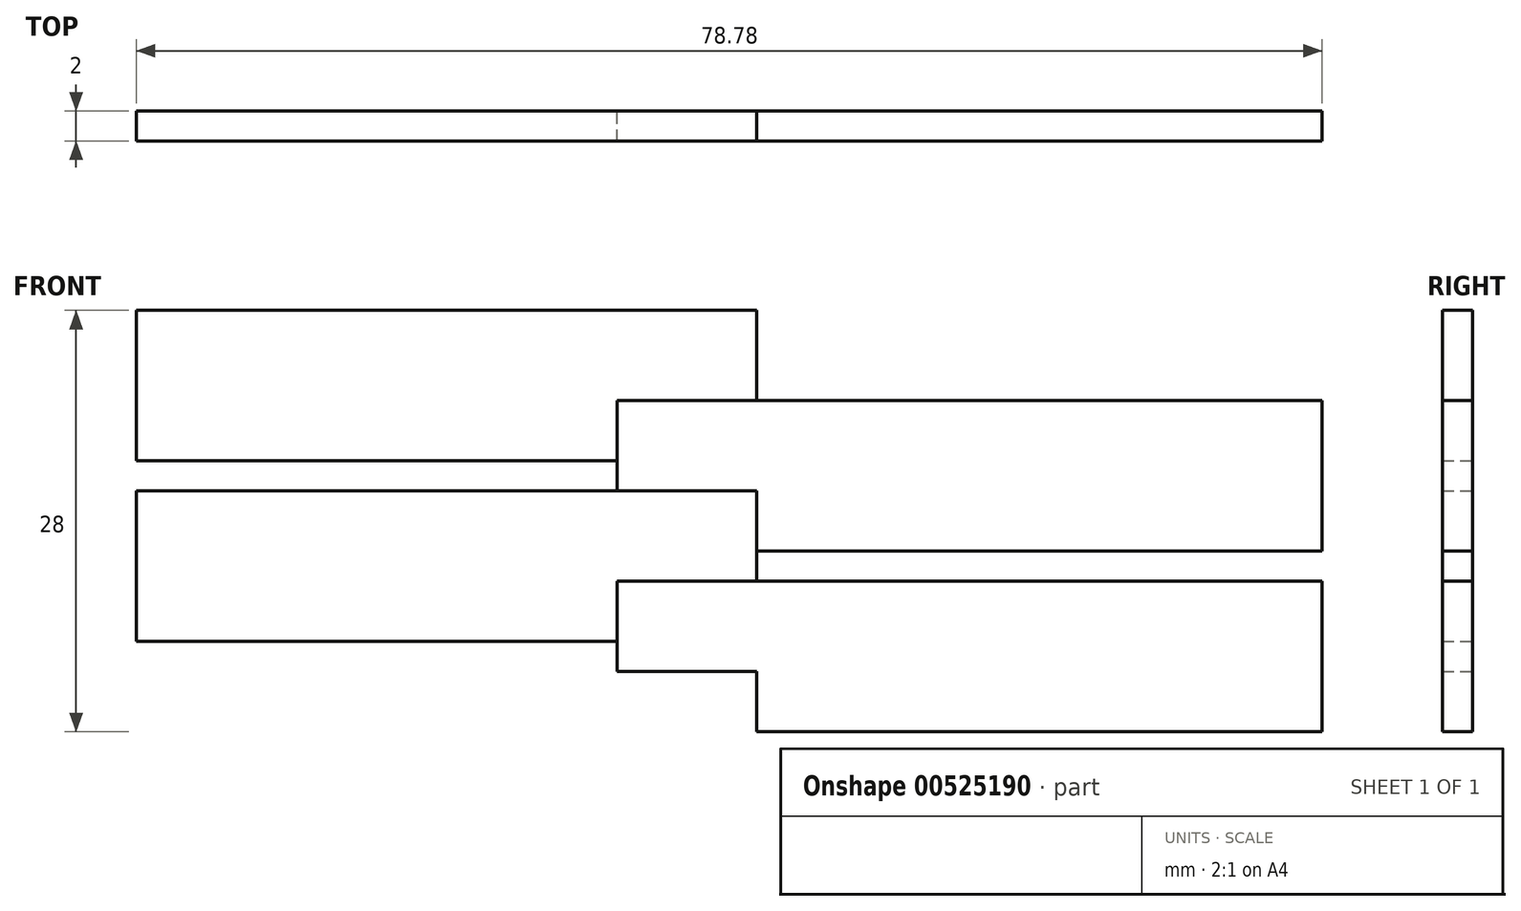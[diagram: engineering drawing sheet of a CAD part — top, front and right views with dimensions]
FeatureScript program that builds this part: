
annotation { "Feature Type Name" : "Feature", "Feature Type Description" : "" }
export const myFeature = defineFeature(function(context is Context, id is Id, definition is map)
    precondition{}
    {
        {
            var Q0;
            Q0=qCreatedBy(makeId("Front.planeOp"),FACE);
            var sketch = newSketch(context, id + "F0", { "sketchPlane" : qUnion([Q0])});
            skLineSegment(sketch, "E0.bottom", {"start": v(-62.98, 181.85) * mm, "end": v(-21.77, 181.85) * mm});
            skLineSegment(sketch, "E0.top", {"start": v(-62.98, 171.85) * mm, "end": v(-21.77, 171.85) * mm});
            skLineSegment(sketch, "E0.left", {"start": v(-62.98, 181.85) * mm, "end": v(-62.98, 171.85) * mm});
            skLineSegment(sketch, "E0.right", {"start": v(-21.77, 181.85) * mm, "end": v(-21.77, 171.85) * mm});
            skLineSegment(sketch, "E1.bottom", {"start": v(-31.04, 187.85) * mm, "end": v(15.8, 187.85) * mm});
            skLineSegment(sketch, "E1.top", {"start": v(-31.04, 177.85) * mm, "end": v(15.8, 177.85) * mm});
            skLineSegment(sketch, "E1.left", {"start": v(-31.04, 187.85) * mm, "end": v(-31.04, 177.85) * mm});
            skLineSegment(sketch, "E1.right", {"start": v(15.8, 187.85) * mm, "end": v(15.8, 177.85) * mm});
            skLineSegment(sketch, "E2.bottom", {"start": v(-62.98, 193.85) * mm, "end": v(-21.77, 193.85) * mm});
            skLineSegment(sketch, "E2.top", {"start": v(-62.98, 183.85) * mm, "end": v(-21.77, 183.85) * mm});
            skLineSegment(sketch, "E2.left", {"start": v(-62.98, 193.85) * mm, "end": v(-62.98, 183.85) * mm});
            skLineSegment(sketch, "E2.right", {"start": v(-21.77, 193.85) * mm, "end": v(-21.77, 183.85) * mm});
            skLineSegment(sketch, "E3.bottom", {"start": v(-31.04, 199.85) * mm, "end": v(15.8, 199.85) * mm});
            skLineSegment(sketch, "E3.top", {"start": v(-31.04, 189.85) * mm, "end": v(15.8, 189.85) * mm});
            skLineSegment(sketch, "E3.left", {"start": v(-31.04, 199.85) * mm, "end": v(-31.04, 189.85) * mm});
            skLineSegment(sketch, "E3.right", {"start": v(15.8, 199.85) * mm, "end": v(15.8, 189.85) * mm});
            skLineSegment(sketch, "E4.bottom", {"start": v(-31.04, 175.85) * mm, "end": v(15.8, 175.85) * mm});
            skLineSegment(sketch, "E4.top", {"start": v(-31.04, 165.85) * mm, "end": v(15.8, 165.85) * mm});
            skLineSegment(sketch, "E4.left", {"start": v(-31.04, 175.85) * mm, "end": v(-31.04, 165.85) * mm});
            skLineSegment(sketch, "E4.right", {"start": v(15.8, 175.85) * mm, "end": v(15.8, 165.85) * mm});
            skLineSegment(sketch, "E5.bottom", {"start": v(-62.98, 169.85) * mm, "end": v(-21.77, 169.85) * mm});
            skLineSegment(sketch, "E5.top", {"start": v(-62.98, 159.85) * mm, "end": v(-21.77, 159.85) * mm});
            skLineSegment(sketch, "E5.left", {"start": v(-62.98, 169.85) * mm, "end": v(-62.98, 159.85) * mm});
            skLineSegment(sketch, "E5.right", {"start": v(-21.77, 169.85) * mm, "end": v(-21.77, 159.85) * mm});
            skLineSegment(sketch, "E6", {"start": v(-21.77, 183.85) * mm, "end": v(-21.77, 181.85) * mm, "construction": true});
            skLineSegment(sketch, "E7", {"start": v(-31.04, 182.85) * mm, "end": v(-21.77, 182.85) * mm, "construction": true});
            skSolve(sketch);
        }
        {
            var Q0;
            {var subQ5=sQuery(id+"F0.wireOp",EDGE,"E0.left");Q0=makeQuery(id+"F0.imprint","IMPRINT",FACE,{"disambiguationData":[TD([[makeQuery(id+"F0.imprint","IMPRINT",EDGE,{"derivedFrom":subQ5}),1.0]])]});}
            var Q1;
            {var subQ0=sQuery(id+"F0.wireOp",EDGE,"E0.right");var subQ1=sQuery(id+"F0.wireOp",EDGE,"E0.bottom");var subQ2=makeQuery(id+"F0.imprint","INTERSECT",VERTEX,{"derivedFrom":[subQ1,subQ0]});Q1=makeQuery(id+"F0.imprint","IMPRINT",FACE,{"disambiguationData":[TD([[makeQuery(id+"F0.imprint","IMPRINT",EDGE,{"disambiguationData":[TD([[subQ2,1.0]])],"derivedFrom":subQ1}),-1.0]])]});}
            var Q2;
            {var subQ0=sQuery(id+"F0.wireOp",EDGE,"E2.left");Q2=makeQuery(id+"F0.imprint","IMPRINT",FACE,{"disambiguationData":[TD([[makeQuery(id+"F0.imprint","IMPRINT",EDGE,{"derivedFrom":subQ0}),1.0]])]});}
            var Q3;
            {var subQ0=sQuery(id+"F0.wireOp",EDGE,"E2.right");var subQ1=sQuery(id+"F0.wireOp",EDGE,"E2.bottom");var subQ2=makeQuery(id+"F0.imprint","INTERSECT",VERTEX,{"derivedFrom":[subQ1,subQ0]});Q3=makeQuery(id+"F0.imprint","IMPRINT",FACE,{"disambiguationData":[TD([[makeQuery(id+"F0.imprint","IMPRINT",EDGE,{"disambiguationData":[TD([[subQ2,1.0]])],"derivedFrom":subQ1}),-1.0]])]});}
            extrude(context, id + "F1", {"entities" : qUnion([Q0, Q1, Q2, Q3]), "depth" : 2 * mm, "offsetDistance" : 25 * mm});
        }
        {
            var Q0;
            {var subQ0=sQuery(id+"F0.wireOp",EDGE,"E1.right");Q0=makeQuery(id+"F0.imprint","IMPRINT",FACE,{"disambiguationData":[TD([[makeQuery(id+"F0.imprint","IMPRINT",EDGE,{"derivedFrom":subQ0}),-1.0]])]});}
            var Q1;
            {var subQ0=sQuery(id+"F0.wireOp",EDGE,"E1.left");var subQ1=sQuery(id+"F0.wireOp",EDGE,"E1.bottom");var subQ2=makeQuery(id+"F0.imprint","INTERSECT",VERTEX,{"derivedFrom":[subQ1,subQ0]});Q1=makeQuery(id+"F0.imprint","IMPRINT",FACE,{"disambiguationData":[TD([[makeQuery(id+"F0.imprint","IMPRINT",EDGE,{"disambiguationData":[TD([[subQ2,-1.0]])],"derivedFrom":subQ1}),-1.0]])]});}
            var Q2;
            {var subQ0=sQuery(id+"F0.wireOp",EDGE,"E4.right");Q2=makeQuery(id+"F0.imprint","IMPRINT",FACE,{"disambiguationData":[TD([[makeQuery(id+"F0.imprint","IMPRINT",EDGE,{"derivedFrom":subQ0}),-1.0]])]});}
            var Q3;
            {var subQ0=sQuery(id+"F0.wireOp",EDGE,"E0.right");var subQ1=sQuery(id+"F0.wireOp",EDGE,"E0.top");var subQ2=makeQuery(id+"F0.imprint","INTERSECT",VERTEX,{"derivedFrom":[subQ1,subQ0]});Q3=makeQuery(id+"F0.imprint","IMPRINT",FACE,{"disambiguationData":[TD([[makeQuery(id+"F0.imprint","IMPRINT",EDGE,{"disambiguationData":[TD([[subQ2,1.0]])],"derivedFrom":subQ1}),1.0]])]});}
            extrude(context, id + "F2", {"entities" : qUnion([Q0, Q1, Q2, Q3]), "depth" : 2 * mm, "offsetDistance" : 25 * mm});
        }
    });
